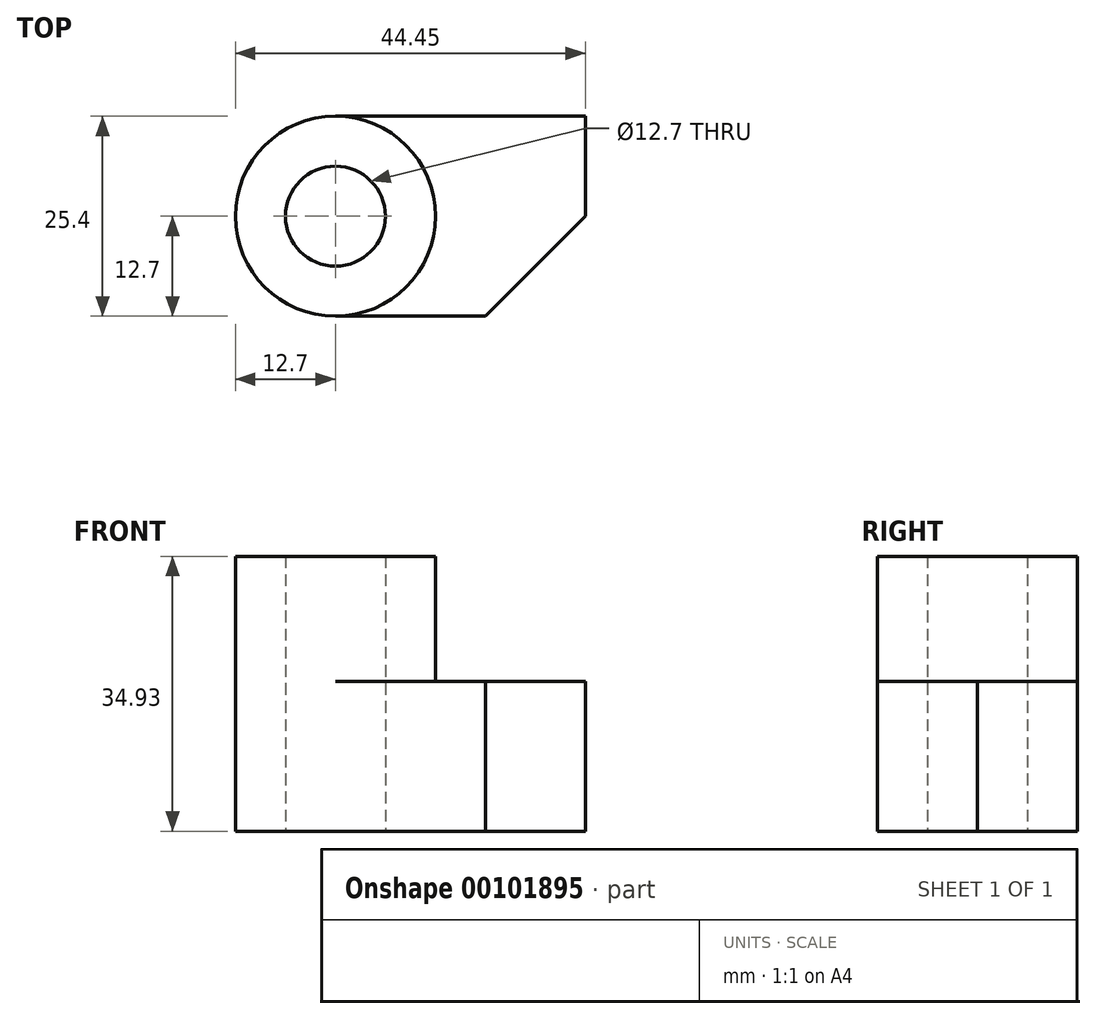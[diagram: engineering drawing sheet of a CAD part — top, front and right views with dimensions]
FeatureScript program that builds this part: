
annotation { "Feature Type Name" : "Feature", "Feature Type Description" : "" }
export const myFeature = defineFeature(function(context is Context, id is Id, definition is map)
    precondition{}
    {
        {
            var Q0;
            Q0=qCreatedBy(makeId("Top.planeOp"),FACE);
            var sketch = newSketch(context, id + "F0", { "sketchPlane" : qUnion([Q0])});
            skCircle(sketch, "E0", {"center": v(0, 0) * mm, "radius": 12.7 * mm});
            skCircle(sketch, "E1", {"center": v(0, 0) * mm, "radius": 6.35 * mm});
            skLineSegment(sketch, "E2", {"start": v(0, 12.7) * mm, "end": v(31.75, 12.7) * mm});
            skLineSegment(sketch, "E3", {"start": v(31.75, 12.7) * mm, "end": v(31.75, -12.7) * mm});
            skLineSegment(sketch, "E4", {"start": v(31.75, -12.7) * mm, "end": v(0, -12.7) * mm});
            skSolve(sketch);
        }
        {
            var Q0;
            Q0=makeQuery(id+"F0.imprint","IMPRINT",FACE,{"disambiguationData":[TD([[makeQuery(id+"F0.imprint","IMPRINT",EDGE,{"derivedFrom":sQuery(id+"F0.wireOp",EDGE,"E1")}),-1.0]])]});
            extrude(context, id + "F1", {"entities" : qUnion([Q0]), "depth" : 25.4 * mm});
        }
        {
            var Q0;
            Q0 = qSketchRegion(id + "F0", true);
            extrude(context, id + "F2", {"entities" : qUnion([Q0]), "operationType" : NewBodyOperationType.ADD, "endBound" : BoundingType.SYMMETRIC, "depth" : 19.05 * mm});
        }
        {
            var Q0;
            Q0=qCreatedBy(makeId("Top.planeOp"),FACE);
            var sketch = newSketch(context, id + "F3", { "sketchPlane" : qUnion([Q0])});
            skLineSegment(sketch, "E5", {"start": v(19.05, -12.7) * mm, "end": v(31.75, 0) * mm});
            skLineSegment(sketch, "E6", {"start": v(31.75, 0) * mm, "end": v(31.75, -12.7) * mm});
            skLineSegment(sketch, "E7", {"start": v(31.75, -12.7) * mm, "end": v(19.05, -12.7) * mm});
            skSolve(sketch);
        }
        {
            var Q0;
            Q0 = qSketchRegion(id + "F3", true);
            extrude(context, id + "F4", {"entities" : qUnion([Q0]), "operationType" : NewBodyOperationType.REMOVE, "endBound" : BoundingType.SYMMETRIC, "depth" : 25.4 * mm});
        }
    });
